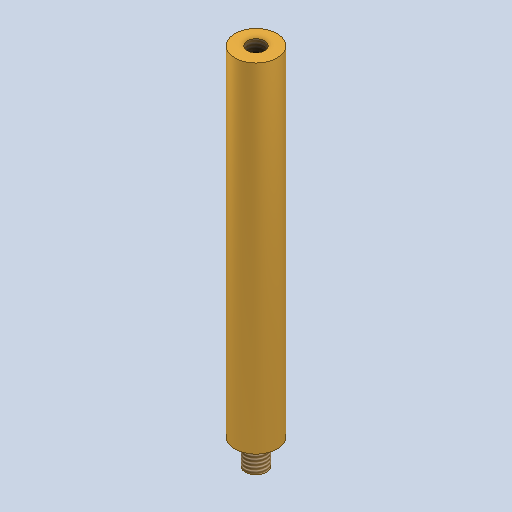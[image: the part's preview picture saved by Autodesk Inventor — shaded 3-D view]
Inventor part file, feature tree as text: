
AUTODESK INVENTOR PART (.ipt)
format: ipt  version: 2023 (Build 270158000, 158)  size: 262,656 bytes
history: native  units: mm
features: sketch x3, extrude x2, other x1, thread x1, hole x1
ambient origin geometry x8: Origin, YZ Plane, XZ Plane, XY Plane, X Axis, Y Axis, Z Axis, Center Point
bodies: Body1 (feature_tree)
feature tree (8):
  other  "Sólido1"
  extrude  "Extrusão1"  Depth=80.0mm TaperAngle=0.0deg
  extrude  "Extrusão3"  Depth=6.0mm TaperAngle=0.0deg
  thread  "Rosca2"  [1 undecoded]
  hole  "Hole1"  [1 undecoded]
  sketch  "Esboço1"  dims[d0=10.0mm d2=80.0mm d3=0.0mm]
  sketch  "Esboço3"  dims[d9=5.0mm d10=6.0mm d11=0.0mm d12=15.0mm d13=0.0mm]
  sketch  "Sketch4"  dims[d14=4.134mm d15=10.0mm d16=4.0mm d17=2.0mm d18=90.0deg d19=14.2mm d20=20.594885mm]
note: 2 required parameter values undecoded (feature->parameter linkage not recoverable at this tier; creation-order binding heuristic only, values carry confidence <= 0.55)
